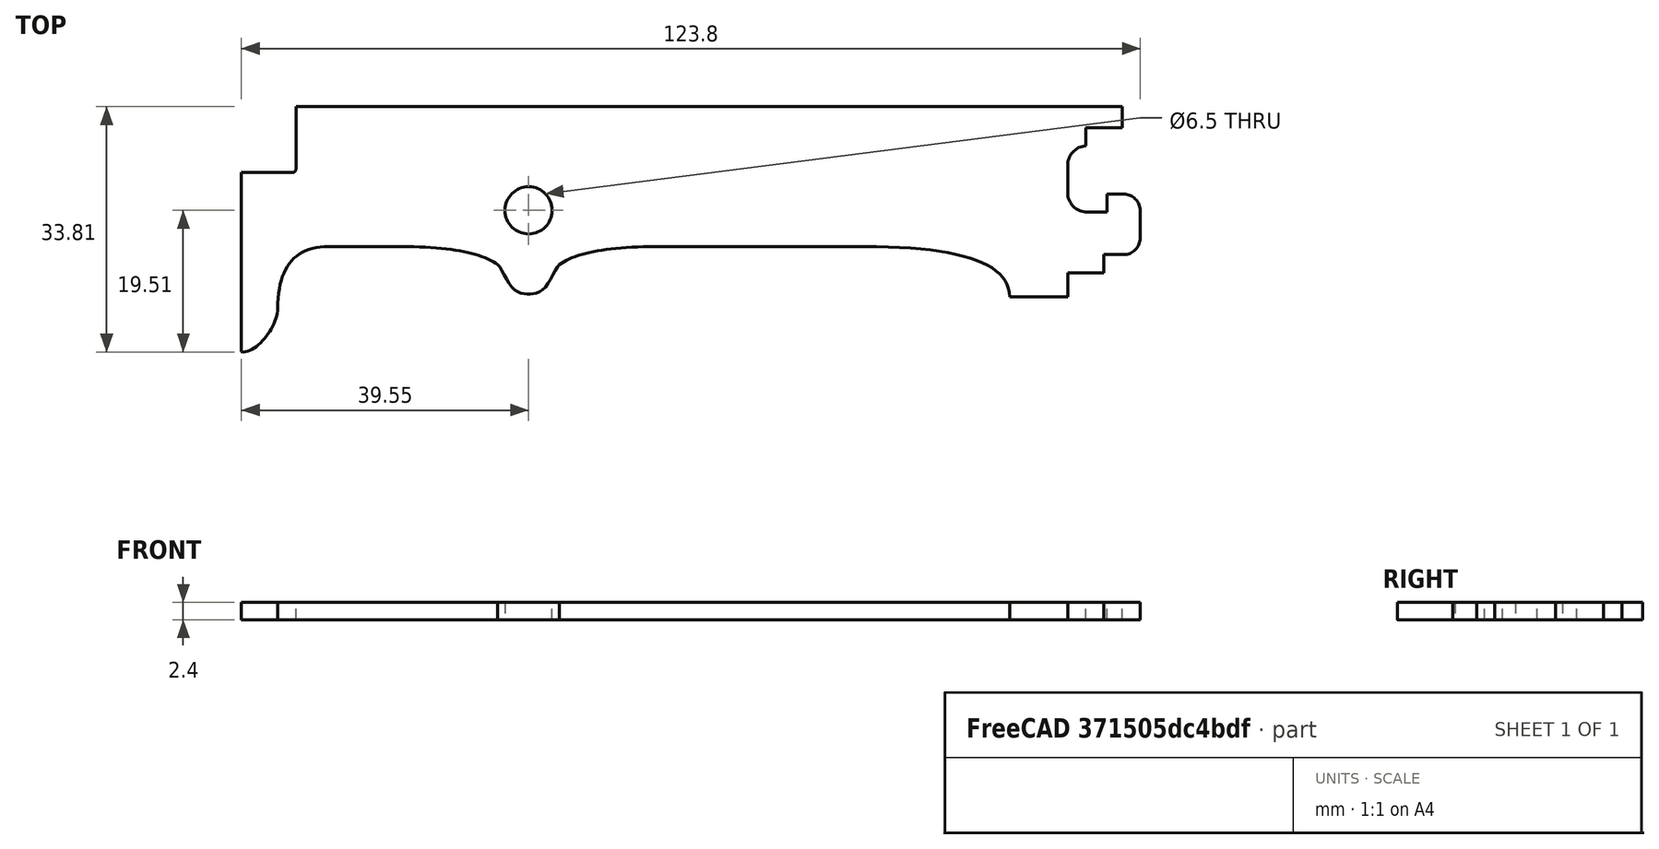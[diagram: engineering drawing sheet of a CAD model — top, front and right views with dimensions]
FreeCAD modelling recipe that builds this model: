
FCSTD DOCUMENT  (FreeCAD 0.19R0.19.2)
Label: v0_13
License: All rights reserved
LicenseURL: http://en.wikipedia.org/wiki/All_rights_reserved
objects: Sketcher::SketchObject×2, Part::Extrusion×1
note: 3 computed .brp shape members not serialized (recipe doc carries the construction recipe); baked Part::Feature solids carry a one-line shape summary decoded from their .brp

FEATURE [Sketcher::SketchObject] Sketch
  FullyConstrained = true
  sketch-geometry (69):
    g0: ArcOfCircle CenterX=-20 CenterY=-14.35 CenterZ=0 NormalX=0 NormalY=0 NormalZ=1 AngleXU=0 Radius=2.3 StartAngle=8e-16 EndAngle=1.5708
    g1: ArcOfCircle CenterX=-20 CenterY=-18.1 CenterZ=0 NormalX=0 NormalY=0 NormalZ=1 AngleXU=0 Radius=2.3 StartAngle=4.71239 EndAngle=6.28319
    g2: LineSegment StartX=-20 StartY=-20.4 StartZ=0 EndX=-22.7 EndY=-20.4 EndZ=0
    g3: LineSegment StartX=-22.7 StartY=-22.9 StartZ=0 EndX=-22.7 EndY=-20.4 EndZ=0
    g4: LineSegment StartX=-17.7 StartY=-14.35 StartZ=0 EndX=-17.7 EndY=-18.1 EndZ=0
    g5: LineSegment StartX=-25.2 StartY=-5.40742 StartZ=0 EndX=-25.2 EndY=-2.9 EndZ=0
    g6: LineSegment StartX=-25.2 StartY=-2.9 StartZ=0 EndX=-20.2 EndY=-2.9 EndZ=0
    g7: LineSegment StartX=-20.2 StartY=-2.9 StartZ=0 EndX=-20.2 EndY=0 EndZ=0
    g8: ArcOfCircle CenterX=-25 CenterY=-8.1 CenterZ=0 NormalX=0 NormalY=0 NormalZ=1 AngleXU=0 Radius=2.7 StartAngle=1.64494 EndAngle=3.14159
    g9: ArcOfCircle CenterX=-25 CenterY=-11.85 CenterZ=0 NormalX=0 NormalY=0 NormalZ=1 AngleXU=0 Radius=2.7 StartAngle=3.14159 EndAngle=4.71239
    g10: LineSegment StartX=-27.7 StartY=-8.1 StartZ=0 EndX=-27.7 EndY=-11.85 EndZ=0
    g11: LineSegment StartX=-25 StartY=-14.55 StartZ=0 EndX=-22.3 EndY=-14.55 EndZ=0
    g12: LineSegment StartX=-22.3 StartY=-12.05 StartZ=0 EndX=-22.3 EndY=-14.55 EndZ=0
    g13: LineSegment StartX=-22.3 StartY=-12.05 StartZ=0 EndX=-20 EndY=-12.05 EndZ=0
    g14: LineSegment StartX=-27.7 StartY=-22.9 StartZ=0 EndX=-22.7 EndY=-22.9 EndZ=0
    g15: LineSegment StartX=-27.7 StartY=-22.9 StartZ=0 EndX=-27.7 EndY=-26.2 EndZ=0
    g16: Circle CenterX=-101.95 CenterY=-14.3 CenterZ=0 NormalX=0 NormalY=0 NormalZ=1 AngleXU=0 Radius=3.25
    g17: LineSegment StartX=-134 StartY=0 StartZ=0 EndX=-20.2 EndY=0 EndZ=0
    g18: LineSegment StartX=-134 StartY=2.68e-14 StartZ=0 EndX=-134 EndY=-8.6 EndZ=0
    g19: LineSegment StartX=-134.5 StartY=-9.1 StartZ=0 EndX=-141.5 EndY=-9.1 EndZ=0
    g20: ArcOfCircle CenterX=-134.5 CenterY=-8.6 CenterZ=0 NormalX=0 NormalY=0 NormalZ=1 AngleXU=0 Radius=0.5 StartAngle=4.71239 EndAngle=6.28319
    g21: Circle CenterX=-97.7 CenterY=-21.8 CenterZ=0 NormalX=0 NormalY=0 NormalZ=1 AngleXU=0 Radius=1
    g22: Circle CenterX=-94.45 CenterY=-19.3 CenterZ=0 NormalX=0 NormalY=0 NormalZ=1 AngleXU=0 Radius=1
    g23: Circle CenterX=-84.45 CenterY=-19.3 CenterZ=0 NormalX=0 NormalY=0 NormalZ=1 AngleXU=0 Radius=1
    g24: BSplineCurve PolesCount=3 KnotsCount=2 Degree=2 IsPeriodic=0
    g25: GeomPoint X=-97.7 Y=-21.8 Z=0
    g26: GeomPoint X=-84.45 Y=-19.3 Z=0
    g27: Circle CenterX=-106.2 CenterY=-21.8 CenterZ=0 NormalX=0 NormalY=0 NormalZ=1 AngleXU=0 Radius=1
    g28: Circle CenterX=-109.45 CenterY=-19.3 CenterZ=0 NormalX=0 NormalY=0 NormalZ=1 AngleXU=0 Radius=1
    g29: Circle CenterX=-119.45 CenterY=-19.3 CenterZ=0 NormalX=0 NormalY=0 NormalZ=1 AngleXU=0 Radius=1
    g30: BSplineCurve PolesCount=3 KnotsCount=2 Degree=2 IsPeriodic=0
    g31: GeomPoint X=-106.2 Y=-21.8 Z=0
    g32: GeomPoint X=-119.45 Y=-19.3 Z=0
    g33: LineSegment StartX=-141.5 StartY=-9.1 StartZ=0 EndX=-141.5 EndY=-33.8 EndZ=0
    g34-g37: Circle x4 (B-spline internal-alignment scaffolding for g38; pole/knot coordinates omitted)
    g38: BSplineCurve PolesCount=4 KnotsCount=2 Degree=3 IsPeriodic=0
    g39: GeomPoint X=-141.5 Y=-33.8 Z=0
    g40: GeomPoint X=-136.5 Y=-27.8 Z=0
    g41: Circle CenterX=-136.5 CenterY=-27.8 CenterZ=0 NormalX=0 NormalY=0 NormalZ=1 AngleXU=0 Radius=1
    g42: Circle CenterX=-136.5 CenterY=-19.3 CenterZ=0 NormalX=0 NormalY=0 NormalZ=1 AngleXU=0 Radius=1
    g43: Circle CenterX=-129.5 CenterY=-19.3 CenterZ=0 NormalX=0 NormalY=0 NormalZ=1 AngleXU=0 Radius=1
    g44: BSplineCurve PolesCount=3 KnotsCount=2 Degree=2 IsPeriodic=0
    g45: GeomPoint X=-136.5 Y=-27.8 Z=0
    g46: GeomPoint X=-129.5 Y=-19.3 Z=0
    g47: LineSegment StartX=-129.5 StartY=-19.3 StartZ=0 EndX=-119.45 EndY=-19.3 EndZ=0
    g48: LineSegment StartX=-35.7 StartY=-26.2 StartZ=0 EndX=-27.7 EndY=-26.2 EndZ=0
    g49: Circle CenterX=-35.7 CenterY=-26.2 CenterZ=0 NormalX=0 NormalY=0 NormalZ=1 AngleXU=0 Radius=1
    g50: Circle CenterX=-35.7 CenterY=-19.3 CenterZ=0 NormalX=0 NormalY=0 NormalZ=1 AngleXU=0 Radius=1
    g51: Circle CenterX=-55.7 CenterY=-19.3 CenterZ=0 NormalX=0 NormalY=0 NormalZ=1 AngleXU=0 Radius=1
    g52: BSplineCurve PolesCount=3 KnotsCount=2 Degree=2 IsPeriodic=0
    g53: GeomPoint X=-35.7 Y=-26.2 Z=0
    g54: GeomPoint X=-55.7 Y=-19.3 Z=0
    g55: LineSegment StartX=-84.45 StartY=-19.3 StartZ=0 EndX=-55.7 EndY=-19.3 EndZ=0
    g56-g62: Circle x7 (B-spline internal-alignment scaffolding for g63; pole/knot coordinates omitted)
    g63: BSplineCurve PolesCount=7 KnotsCount=5 Degree=3 IsPeriodic=0
    g64-g68: GeomPoint x5 (B-spline internal-alignment scaffolding for g63; pole/knot coordinates omitted)
  constraints (111):
    c: Block(g1)
    c: Block(g0)
    c: Coincident(g2,g1)
    c: Horizontal(g2)
    c: Vertical(g3)
    c: Coincident(g3,g2)
    c: Coincident(g4,g0)
    c: Coincident(g4,g1)
    c: Vertical(g4)
    c: Vertical(g5)
    c: Block(g5)
    c: Coincident(g6,g5)
    c: Horizontal(g6)
    c: Vertical(g7)
    c: Block(g7)
    c: Block(g6)
    c: Coincident(g8,g5)
    c: Block(g9)
    c: Coincident(g10,g8)
    c: Coincident(g10,g9)
    c: Vertical(g10)
    c: Block(g10)
    c: Coincident(g11,g9)
    c: Horizontal(g11)
    c: Vertical(g12)
    c: Coincident(g12,g11)
    c: Block(g12)
    c: Coincident(g13,g0)
    c: Horizontal(g13)
    c: Block(g13)
    c: Coincident(g14,g3)
    c: Horizontal(g14)
    c: Block(g14)
    c: Coincident(g15,g14)
    c: Vertical(g15)
    c: Block(g16)
    c: Coincident(g17,g7)
    c: Horizontal(g17)
    c: Vertical(g18)
    c: Distance(g18) = 8.6
    c: Horizontal(g19)
    c: Distance(g19) = 7
    c: Coincident(g20,g18)
    c: Coincident(g20,g19)
    c: Block(g20)
    c: Block(g17)
    c: Weight(g21) = 1
    c: Equal(g21,g22)
    c: Equal(g21,g23)
    c: InternalAlignment(g21,g24)
    c: InternalAlignment(g22,g24)
    c: InternalAlignment(g23,g24)
    c: InternalAlignment(g25,g24)
    c: InternalAlignment(g26,g24)
    c: Weight(g27) = 1
    c: Equal(g27,g28)
    c: Equal(g27,g29)
    c: InternalAlignment(g27,g30)
    c: InternalAlignment(g28,g30)
    c: InternalAlignment(g29,g30)
    c: InternalAlignment(g31,g30)
    c: InternalAlignment(g32,g30)
    c: Block(g30)
    c: Block(g24)
    c: Coincident(g33,g19)
    c: Vertical(g33)
    c: Block(g33)
    c: Coincident(g38,g33)
    c: Weight(g34) = 1
    c: Equal(g34,g35)
    c: Equal(g34,g36)
    c: Equal(g34,g37)
    c: InternalAlignment(g34-g37 -> g38) x4
    c: InternalAlignment(g39,g38)
    c: InternalAlignment(g40,g38)
    c: Weight(g41) = 1
    c: Equal(g41,g42)
    c: Equal(g41,g43)
    c: InternalAlignment(g41,g44)
    c: InternalAlignment(g42,g44)
    c: InternalAlignment(g43,g44)
    c: InternalAlignment(g45,g44)
    c: InternalAlignment(g46,g44)
    c: Block(g38)
    c: Block(g44)
    c: Coincident(g47,g44)
    c: Coincident(g47,g30)
    c: Horizontal(g47)
    c: Horizontal(g48)
    c: Distance(g48) = 8
    c: Block(g48)
    c: Block(g15)
    c: Block(g8)
    c: Coincident(g52,g48)
    c: Weight(g49) = 1
    c: Equal(g49,g50)
    c: Equal(g49,g51)
    c: InternalAlignment(g49,g52)
    c: InternalAlignment(g50,g52)
    c: InternalAlignment(g51,g52)
    c: InternalAlignment(g53,g52)
    c: InternalAlignment(g54,g52)
    c: Block(g52)
    c: Coincident(g55,g24)
    c: Coincident(g55,g52)
    c: Horizontal(g55)
    c: Weight(g56) = 1
    c: Equal(g56, g57-g62) x6
    c: InternalAlignment(g56-g62 -> g63) x7
    c: InternalAlignment(g64-g68 -> g63) x5
    c: Block(g63)
FEATURE [Part::Extrusion] Extrude
  Base = -> Sketch
  Dir = (0,0,1)
  DirMode = 2
  FaceMakerClass = Part::FaceMakerBullseye
  LengthFwd = 2.4
  LengthRev = 0
  Solid = true
  Symmetric = false
FEATURE [Sketcher::SketchObject] Sketch001
  FullyConstrained = true
  sketch-geometry (75):
    g0: ArcOfCircle CenterX=-20 CenterY=-14.35 CenterZ=0 NormalX=0 NormalY=0 NormalZ=1 AngleXU=0 Radius=2.3 StartAngle=8e-16 EndAngle=1.5708
    g1: ArcOfCircle CenterX=-20 CenterY=-18.1 CenterZ=0 NormalX=0 NormalY=0 NormalZ=1 AngleXU=0 Radius=2.3 StartAngle=4.71239 EndAngle=6.28319
    g2: LineSegment StartX=-20 StartY=-20.4 StartZ=0 EndX=-22.7 EndY=-20.4 EndZ=0
    g3: LineSegment StartX=-22.7 StartY=-22.9 StartZ=0 EndX=-22.7 EndY=-20.4 EndZ=0
    g4: LineSegment StartX=-17.7 StartY=-14.35 StartZ=0 EndX=-17.7 EndY=-18.1 EndZ=0
    g5: LineSegment StartX=-25.2 StartY=-5.40742 StartZ=0 EndX=-25.2 EndY=-2.9 EndZ=0
    g6: LineSegment StartX=-25.2 StartY=-2.9 StartZ=0 EndX=-20.2 EndY=-2.9 EndZ=0
    g7: LineSegment StartX=-20.2 StartY=-2.9 StartZ=0 EndX=-20.2 EndY=0 EndZ=0
    g8: ArcOfCircle CenterX=-25 CenterY=-8.1 CenterZ=0 NormalX=0 NormalY=0 NormalZ=1 AngleXU=0 Radius=2.7 StartAngle=1.64494 EndAngle=3.14159
    g9: ArcOfCircle CenterX=-25 CenterY=-11.85 CenterZ=0 NormalX=0 NormalY=0 NormalZ=1 AngleXU=0 Radius=2.7 StartAngle=3.14159 EndAngle=4.71239
    g10: LineSegment StartX=-27.7 StartY=-8.1 StartZ=0 EndX=-27.7 EndY=-11.85 EndZ=0
    g11: LineSegment StartX=-25 StartY=-14.55 StartZ=0 EndX=-22.3 EndY=-14.55 EndZ=0
    g12: LineSegment StartX=-22.3 StartY=-12.05 StartZ=0 EndX=-22.3 EndY=-14.55 EndZ=0
    g13: LineSegment StartX=-22.3 StartY=-12.05 StartZ=0 EndX=-20 EndY=-12.05 EndZ=0
    g14: LineSegment StartX=-27.7 StartY=-22.9 StartZ=0 EndX=-22.7 EndY=-22.9 EndZ=0
    g15: LineSegment StartX=-27.7 StartY=-22.9 StartZ=0 EndX=-27.7 EndY=-26.2 EndZ=0
    g16: Circle CenterX=-101.95 CenterY=-14.3 CenterZ=0 NormalX=0 NormalY=0 NormalZ=1 AngleXU=0 Radius=3.25
    g17: LineSegment StartX=-134 StartY=0 StartZ=0 EndX=-134 EndY=-8.6 EndZ=0
    g18: LineSegment StartX=-134.5 StartY=-9.1 StartZ=0 EndX=-141.5 EndY=-9.1 EndZ=0
    g19: ArcOfCircle CenterX=-134.5 CenterY=-8.6 CenterZ=0 NormalX=0 NormalY=0 NormalZ=1 AngleXU=0 Radius=0.5 StartAngle=4.71239 EndAngle=6.28319
    g20: Circle CenterX=-97.7 CenterY=-21.8 CenterZ=0 NormalX=0 NormalY=0 NormalZ=1 AngleXU=0 Radius=1
    g21: Circle CenterX=-94.45 CenterY=-19.3 CenterZ=0 NormalX=0 NormalY=0 NormalZ=1 AngleXU=0 Radius=1
    g22: Circle CenterX=-84.45 CenterY=-19.3 CenterZ=0 NormalX=0 NormalY=0 NormalZ=1 AngleXU=0 Radius=1
    g23: BSplineCurve PolesCount=3 KnotsCount=2 Degree=2 IsPeriodic=0
    g24: GeomPoint X=-97.7 Y=-21.8 Z=0
    g25: GeomPoint X=-84.45 Y=-19.3 Z=0
    g26: Circle CenterX=-106.2 CenterY=-21.8 CenterZ=0 NormalX=0 NormalY=0 NormalZ=1 AngleXU=0 Radius=1
    g27: Circle CenterX=-109.45 CenterY=-19.3 CenterZ=0 NormalX=0 NormalY=0 NormalZ=1 AngleXU=0 Radius=1
    g28: Circle CenterX=-119.45 CenterY=-19.3 CenterZ=0 NormalX=0 NormalY=0 NormalZ=1 AngleXU=0 Radius=1
    g29: BSplineCurve PolesCount=3 KnotsCount=2 Degree=2 IsPeriodic=0
    g30: GeomPoint X=-106.2 Y=-21.8 Z=0
    g31: GeomPoint X=-119.45 Y=-19.3 Z=0
    g32: LineSegment StartX=-141.5 StartY=-9.1 StartZ=0 EndX=-141.5 EndY=-33.8 EndZ=0
    g33-g36: Circle x4 (B-spline internal-alignment scaffolding for g37; pole/knot coordinates omitted)
    g37: BSplineCurve PolesCount=4 KnotsCount=2 Degree=3 IsPeriodic=0
    g38: GeomPoint X=-141.5 Y=-33.8 Z=0
    g39: GeomPoint X=-136.5 Y=-27.8 Z=0
    g40: Circle CenterX=-136.5 CenterY=-27.8 CenterZ=0 NormalX=0 NormalY=0 NormalZ=1 AngleXU=0 Radius=1
    g41: Circle CenterX=-136.5 CenterY=-19.3 CenterZ=0 NormalX=0 NormalY=0 NormalZ=1 AngleXU=0 Radius=1
    g42: Circle CenterX=-129.5 CenterY=-19.3 CenterZ=0 NormalX=0 NormalY=0 NormalZ=1 AngleXU=0 Radius=1
    g43: BSplineCurve PolesCount=3 KnotsCount=2 Degree=2 IsPeriodic=0
    g44: GeomPoint X=-136.5 Y=-27.8 Z=0
    g45: GeomPoint X=-129.5 Y=-19.3 Z=0
    g46: LineSegment StartX=-129.5 StartY=-19.3 StartZ=0 EndX=-119.45 EndY=-19.3 EndZ=0
    g47: LineSegment StartX=-35.7 StartY=-26.2 StartZ=0 EndX=-27.7 EndY=-26.2 EndZ=0
    g48: Circle CenterX=-35.7 CenterY=-26.2 CenterZ=0 NormalX=0 NormalY=0 NormalZ=1 AngleXU=0 Radius=1
    g49: Circle CenterX=-35.7 CenterY=-19.3 CenterZ=0 NormalX=0 NormalY=0 NormalZ=1 AngleXU=0 Radius=1
    g50: Circle CenterX=-55.7 CenterY=-19.3 CenterZ=0 NormalX=0 NormalY=0 NormalZ=1 AngleXU=0 Radius=1
    g51: BSplineCurve PolesCount=3 KnotsCount=2 Degree=2 IsPeriodic=0
    g52: GeomPoint X=-35.7 Y=-26.2 Z=0
    g53: GeomPoint X=-55.7 Y=-19.3 Z=0
    g54: LineSegment StartX=-84.45 StartY=-19.3 StartZ=0 EndX=-55.7 EndY=-19.3 EndZ=0
    g55-g61: Circle x7 (B-spline internal-alignment scaffolding for g62; pole/knot coordinates omitted)
    g62: BSplineCurve PolesCount=7 KnotsCount=5 Degree=3 IsPeriodic=0
    g63-g67: GeomPoint x5 (B-spline internal-alignment scaffolding for g62; pole/knot coordinates omitted)
    g68: LineSegment StartX=-131 StartY=0 StartZ=0 EndX=-131 EndY=-3 EndZ=0
    g69: LineSegment StartX=-134 StartY=0 StartZ=0 EndX=-20.2 EndY=0 EndZ=0
    g70: LineSegment StartX=-131 StartY=-3 StartZ=0 EndX=-35.7 EndY=-3 EndZ=0
    g71: LineSegment StartX=-35.7 StartY=-3 StartZ=0 EndX=-35.7 EndY=-16.3 EndZ=0
    g72: LineSegment StartX=-35.7 StartY=-16.3 StartZ=0 EndX=-97.7 EndY=-16.3 EndZ=0
    g73: LineSegment StartX=-129.5 StartY=-16.3 StartZ=0 EndX=-106.2 EndY=-16.3 EndZ=0
    g74: ArcOfCircle CenterX=-101.95 CenterY=-14.3 CenterZ=0 NormalX=0 NormalY=0 NormalZ=1 AngleXU=0 Radius=4.69707 StartAngle=3.58144 EndAngle=5.84334
  constraints (128):
    c: Block(g1)
    c: Block(g0)
    c: Coincident(g2,g1)
    c: Horizontal(g2)
    c: Vertical(g3)
    c: Coincident(g3,g2)
    c: Coincident(g4,g0)
    c: Coincident(g4,g1)
    c: Vertical(g4)
    c: Vertical(g5)
    c: Block(g5)
    c: Coincident(g6,g5)
    c: Horizontal(g6)
    c: Vertical(g7)
    c: Block(g7)
    c: Block(g6)
    c: Coincident(g8,g5)
    c: Block(g9)
    c: Coincident(g10,g8)
    c: Coincident(g10,g9)
    c: Vertical(g10)
    c: Block(g10)
    c: Coincident(g11,g9)
    c: Horizontal(g11)
    c: Vertical(g12)
    c: Coincident(g12,g11)
    c: Block(g12)
    c: Coincident(g13,g0)
    c: Horizontal(g13)
    c: Block(g13)
    c: Coincident(g14,g3)
    c: Horizontal(g14)
    c: Block(g14)
    c: Coincident(g15,g14)
    c: Vertical(g15)
    c: Block(g16)
    c: Vertical(g17)
    c: Distance(g17) = 8.6
    c: Horizontal(g18)
    c: Distance(g18) = 7
    c: Coincident(g19,g17)
    c: Coincident(g19,g18)
    c: Block(g19)
    c: Weight(g20) = 1
    c: Equal(g20,g21)
    c: Equal(g20,g22)
    c: InternalAlignment(g20,g23)
    c: InternalAlignment(g21,g23)
    c: InternalAlignment(g22,g23)
    c: InternalAlignment(g24,g23)
    c: InternalAlignment(g25,g23)
    c: Weight(g26) = 1
    c: Equal(g26,g27)
    c: Equal(g26,g28)
    c: InternalAlignment(g26,g29)
    c: InternalAlignment(g27,g29)
    c: InternalAlignment(g28,g29)
    c: InternalAlignment(g30,g29)
    c: InternalAlignment(g31,g29)
    c: Block(g23)
    c: Coincident(g32,g18)
    c: Vertical(g32)
    c: Block(g32)
    c: Coincident(g37,g32)
    c: Weight(g33) = 1
    c: Equal(g33,g34)
    c: Equal(g33,g35)
    c: Equal(g33,g36)
    c: InternalAlignment(g33-g36 -> g37) x4
    c: InternalAlignment(g38,g37)
    c: InternalAlignment(g39,g37)
    c: Weight(g40) = 1
    c: Equal(g40,g41)
    c: Equal(g40,g42)
    c: InternalAlignment(g40,g43)
    c: InternalAlignment(g41,g43)
    c: InternalAlignment(g42,g43)
    c: InternalAlignment(g44,g43)
    c: InternalAlignment(g45,g43)
    c: Block(g37)
    c: Coincident(g46,g43)
    c: Coincident(g46,g29)
    c: Horizontal(g46)
    c: Horizontal(g47)
    c: Distance(g47) = 8
    c: Block(g47)
    c: Block(g15)
    c: Block(g8)
    c: Coincident(g51,g47)
    c: Weight(g48) = 1
    c: Equal(g48,g49)
    c: Equal(g48,g50)
    c: InternalAlignment(g48,g51)
    c: InternalAlignment(g49,g51)
    c: InternalAlignment(g50,g51)
    c: InternalAlignment(g52,g51)
    c: InternalAlignment(g53,g51)
    c: Block(g51)
    c: Coincident(g54,g23)
    c: Coincident(g54,g51)
    c: Horizontal(g54)
    c: Weight(g55) = 1
    c: Equal(g55, g56-g61) x6
    c: InternalAlignment(g55-g61 -> g62) x7
    c: InternalAlignment(g63-g67 -> g62) x5
    c: Block(g62)
    c: Vertical(g68)
    c: Distance(g68) = 3
    c: Coincident(g69,g17)
    c: Coincident(g69,g7)
    c: Horizontal(g69)
    c: Coincident(g70,g68)
    c: Horizontal(g70)
    c: Block(g70)
    c: Coincident(g71,g70)
    c: Vertical(g71)
    c: Block(g71)
    c: Coincident(g72,g71)
    c: Horizontal(g72)
    c: Horizontal(g73)
    c: Block(g72)
    c: Coincident(g74,g16)
    c: Coincident(g74,g72)
    c: Coincident(g74,g73)
    c: Block(g74)
    c: Distance(g73) = 23.3
    c: Block(g29)
    c: Block(g43)
